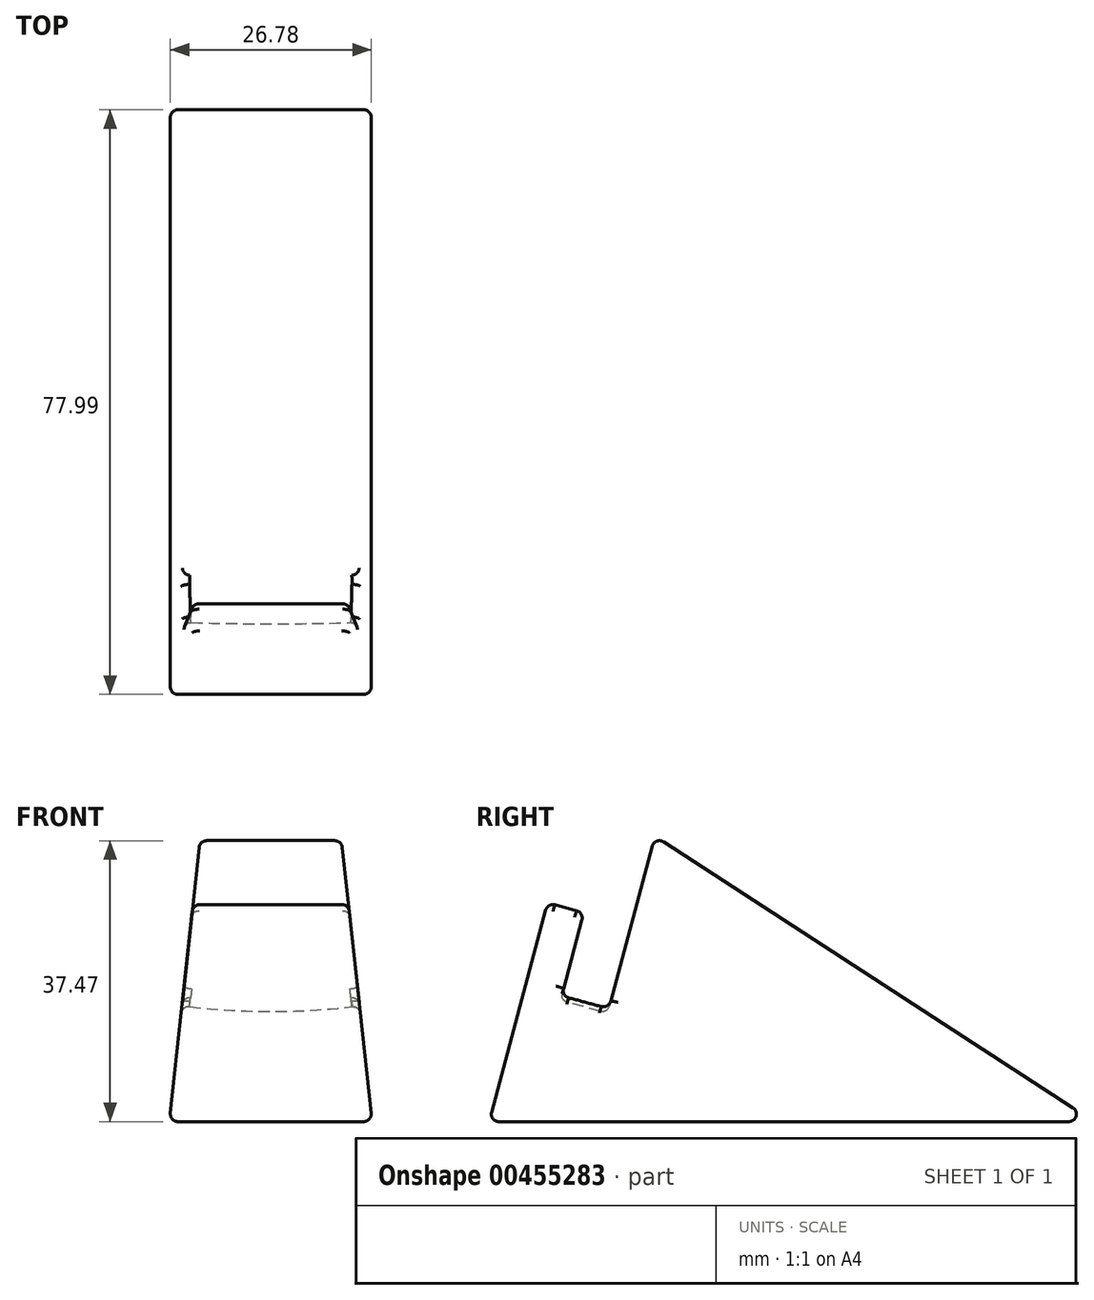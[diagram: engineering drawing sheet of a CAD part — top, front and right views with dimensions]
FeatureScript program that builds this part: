
annotation { "Feature Type Name" : "Feature", "Feature Type Description" : "" }
export const myFeature = defineFeature(function(context is Context, id is Id, definition is map)
    precondition{}
    {
        {
            var Q0;
            Q0=qCreatedBy(makeId("Right.planeOp"),FACE);
            var sketch = newSketch(context, id + "F0", { "sketchPlane" : qUnion([Q0])});
            skLineSegment(sketch, "E0.bottom", {"start": v(0, 0) * mm, "end": v(80.67, 0) * mm});
            skLineSegment(sketch, "E0.top", {"start": v(10.35, 38.64) * mm, "end": v(21.22, 38.64) * mm});
            skLineSegment(sketch, "E1", {"start": v(0, 0) * mm, "end": v(10.35, 38.64) * mm});
            skPoint(sketch, "E2", {"position": v(15.35, 38.64) * mm});
            skLineSegment(sketch, "E3", {"start": v(21.22, 38.64) * mm, "end": v(80.67, 0) * mm});
            skSolve(sketch);
        }
        {
            var Q0;
            Q0=makeQuery(id+"F0.imprint","IMPRINT",FACE,{"disambiguationData":[TD([[makeQuery(id+"F0.imprint","IMPRINT",EDGE,{"derivedFrom":sQuery(id+"F0.wireOp",EDGE,"E0.bottom")}),1.0]])]});
            extrude(context, id + "F1", {"entities" : qUnion([Q0]), "depth" : 27 * mm});
        }
        {
            var Q0;
            Q0=makeQuery(id+"F1.opExtrude","SWEPT_FACE",FACE,{"disambiguationData":[OSD([sQuery(id+"F0.wireOp",EDGE,"E1")])]});
            cPlane(context, id + "F2", {"entities" : qUnion([Q0]), "cplaneType" : CPlaneType.OFFSET, "offset" : 5 * mm, "oppositeDirection" : true, "width" : 150 * mm, "height" : 150 * mm});
        }
        {
            var Q0;
            Q0=qCreatedBy(id+"F2.planeOp",FACE);
            var sketch = newSketch(context, id + "F3", { "sketchPlane" : qUnion([Q0])});
            skPoint(sketch, "E4.0", {"position": v(13.5, 0) * mm});
            skLineSegment(sketch, "E5", {"start": v(13.5, 0) * mm, "end": v(13.5, 110) * mm, "construction": true});
            skCircle(sketch, "E6", {"center": v(13.5, 110) * mm, "radius": 91.94 * mm});
            skSolve(sketch);
        }
        {
            var Q0;
            Q0 = qSketchRegion(id + "F3", true);
            extrude(context, id + "F4", {"entities" : qUnion([Q0]), "operationType" : NewBodyOperationType.REMOVE, "oppositeDirection" : true, "depth" : 6.5 * mm});
        }
        {
            var Q0;
            Q0=makeQuery(id+"F1.opExtrude","CAP_FACE",FACE,{"disambiguationData":[OSD([sQuery(id+"F0.wireOp",EDGE,"E0.bottom"),sQuery(id+"F0.wireOp",EDGE,"E0.top"),sQuery(id+"F0.wireOp",EDGE,"E1"),sQuery(id+"F0.wireOp",EDGE,"E3")])],"isStart":true});
            var sketch = newSketch(context, id + "F5", { "sketchPlane" : qUnion([Q0])});
            skLineSegment(sketch, "E7", {"start": v(-12.65, 27.87) * mm, "end": v(-7.82, 29.17) * mm});
            skLineSegment(sketch, "E8", {"start": v(-12.65, 27.87) * mm, "end": v(-18.68, 34.78) * mm});
            skLineSegment(sketch, "E9", {"start": v(-18.68, 34.78) * mm, "end": v(-16.11, 47.32) * mm});
            skLineSegment(sketch, "E10", {"start": v(-16.11, 47.32) * mm, "end": v(-7.28, 43.61) * mm});
            skLineSegment(sketch, "E11", {"start": v(-7.28, 43.61) * mm, "end": v(-5.57, 30.5) * mm});
            skLineSegment(sketch, "E12", {"start": v(-5.57, 30.5) * mm, "end": v(-7.82, 29.17) * mm});
            skSolve(sketch);
        }
        {
            var Q0;
            {var subQ4=sQuery(id+"F5.wireOp",EDGE,"E8");Q0=makeQuery(id+"F5.imprint","IMPRINT",FACE,{"disambiguationData":[TD([[makeQuery(id+"F5.imprint","IMPRINT",EDGE,{"derivedFrom":subQ4}),-1.0]])]});}
            var Q1;
            {var subQ0=sQuery(id+"F5.wireOp",EDGE,"E7");Q1=makeQuery(id+"F5.imprint","IMPRINT",FACE,{"disambiguationData":[TD([[makeQuery(id+"F5.imprint","IMPRINT",EDGE,{"derivedFrom":subQ0}),1.0]])]});}
            extrude(context, id + "F6", {"entities" : qUnion([Q0, Q1]), "operationType" : NewBodyOperationType.REMOVE, "oppositeDirection" : true, "depth" : 43.7 * mm});
        }
        {
            var Q0;
            Q0=qCreatedBy(makeId("Front.planeOp"),FACE);
            var sketch = newSketch(context, id + "F7", { "sketchPlane" : qUnion([Q0])});
            skLineSegment(sketch, "E13", {"start": v(0, 0) * mm, "end": v(5.54, 51.24) * mm});
            skPoint(sketch, "E14.0", {"position": v(13.5, 38.06) * mm});
            skLineSegment(sketch, "E15", {"start": v(13.5, 38.06) * mm, "end": v(13.5, -10) * mm, "construction": true});
            skLineSegment(sketch, "E16.MirrorCS", {"start": v(27, 0) * mm, "end": v(21.46, 51.24) * mm});
            skLineSegment(sketch, "E17", {"start": v(5.54, 51.24) * mm, "end": v(-18.57, 42.6) * mm, "construction": true});
            skLineSegment(sketch, "E18", {"start": v(5.54, 51.24) * mm, "end": v(-20.23, 29.38) * mm});
            skLineSegment(sketch, "E19", {"start": v(-20.23, 29.38) * mm, "end": v(-22.2, -20.87) * mm});
            skLineSegment(sketch, "E20", {"start": v(-22.2, -20.87) * mm, "end": v(0, 0) * mm});
            skLineSegment(sketch, "E21", {"start": v(27, 0) * mm, "end": v(40.61, -9.3) * mm});
            skLineSegment(sketch, "E22", {"start": v(40.61, -9.3) * mm, "end": v(49.87, 59.14) * mm});
            skLineSegment(sketch, "E23", {"start": v(49.87, 59.14) * mm, "end": v(21.46, 51.24) * mm});
            skSolve(sketch);
        }
        {
            var Q0;
            Q0=makeQuery(id+"F7.imprint","IMPRINT",FACE,{"disambiguationData":[TD([[makeQuery(id+"F7.imprint","IMPRINT",EDGE,{"derivedFrom":sQuery(id+"F7.wireOp",EDGE,"E16.MirrorCS")}),-1.0]])]});
            var Q1;
            Q1=makeQuery(id+"F7.imprint","IMPRINT",FACE,{"disambiguationData":[TD([[makeQuery(id+"F7.imprint","IMPRINT",EDGE,{"derivedFrom":sQuery(id+"F7.wireOp",EDGE,"E13")}),1.0]])]});
            extrude(context, id + "F8", {"entities" : qUnion([Q0, Q1]), "operationType" : NewBodyOperationType.REMOVE, "oppositeDirection" : true, "depth" : 96 * mm});
        }
        {
            var Q0;
            Q0=makeQuery(id+"F8.boolean.opBoolean","INTERSECT",EDGE,{"derivedFrom":[makeQuery(id+"F4.boolean.opBoolean","COPY",FACE,{"derivedFrom":makeQuery(id+"F4.opExtrude","CAP_FACE",FACE,{"disambiguationData":[OSD([sQuery(id+"F3.wireOp",EDGE,"E6")])],"isStart":false})}),makeQuery(id+"F8.opExtrude","SWEPT_FACE",FACE,{"disambiguationData":[OSD([sQuery(id+"F7.wireOp",EDGE,"E13")])]})]});
            var Q1;
            Q1=makeQuery(id+"F4.boolean.opBoolean","INTERSECT",EDGE,{"derivedFrom":[makeQuery(id+"F1.opExtrude","SWEPT_FACE",FACE,{"disambiguationData":[OSD([sQuery(id+"F0.wireOp",EDGE,"E3")])]}),makeQuery(id+"F4.opExtrude","CAP_FACE",FACE,{"disambiguationData":[OSD([sQuery(id+"F3.wireOp",EDGE,"E6")])],"isStart":false})]});
            var Q2;
            Q2=makeQuery(id+"F1.opExtrude","SWEPT_FACE",FACE,{"disambiguationData":[OSD([sQuery(id+"F0.wireOp",EDGE,"E3")])]});
            var Q3;
            Q3=makeQuery(id+"F4.boolean.opBoolean","COPY",FACE,{"derivedFrom":makeQuery(id+"F4.opExtrude","CAP_FACE",FACE,{"disambiguationData":[OSD([sQuery(id+"F3.wireOp",EDGE,"E6")])],"isStart":false})});
            var Q4;
            Q4=makeQuery(id+"F8.boolean.opBoolean","INTERSECT",EDGE,{"derivedFrom":[makeQuery(id+"F4.boolean.opBoolean","COPY",FACE,{"derivedFrom":makeQuery(id+"F4.opExtrude","CAP_FACE",FACE,{"disambiguationData":[OSD([sQuery(id+"F3.wireOp",EDGE,"E6")])],"isStart":true})}),makeQuery(id+"F8.opExtrude","SWEPT_FACE",FACE,{"disambiguationData":[OSD([sQuery(id+"F7.wireOp",EDGE,"E16.MirrorCS")])]})]});
            var Q5;
            Q5=makeQuery(id+"F8.boolean.opBoolean","INTERSECT",EDGE,{"derivedFrom":[makeQuery(id+"F4.boolean.opBoolean","COPY",FACE,{"derivedFrom":makeQuery(id+"F4.opExtrude","CAP_FACE",FACE,{"disambiguationData":[OSD([sQuery(id+"F3.wireOp",EDGE,"E6")])],"isStart":false})}),makeQuery(id+"F8.opExtrude","SWEPT_FACE",FACE,{"disambiguationData":[OSD([sQuery(id+"F7.wireOp",EDGE,"E16.MirrorCS")])]})]});
            var Q6;
            Q6=makeQuery(id+"F8.boolean.opBoolean","COPY",FACE,{"derivedFrom":makeQuery(id+"F8.opExtrude","SWEPT_FACE",FACE,{"disambiguationData":[OSD([sQuery(id+"F7.wireOp",EDGE,"E16.MirrorCS")])]})});
            var Q7;
            Q7=makeQuery(id+"F1.opExtrude","SWEPT_EDGE",EDGE,{"disambiguationData":[OSD([sQuery(id+"F0.wireOp",EDGE,"E0.bottom"),sQuery(id+"F0.wireOp",EDGE,"E1")])]});
            var Q8;
            Q8=makeQuery(id+"F1.opExtrude","SWEPT_FACE",FACE,{"disambiguationData":[OSD([sQuery(id+"F0.wireOp",EDGE,"E0.bottom")])]});
            var Q9;
            Q9=makeQuery(id+"F8.boolean.opBoolean","INTERSECT",EDGE,{"derivedFrom":[makeQuery(id+"F1.opExtrude","SWEPT_FACE",FACE,{"disambiguationData":[OSD([sQuery(id+"F0.wireOp",EDGE,"E1")])]}),makeQuery(id+"F8.opExtrude","SWEPT_FACE",FACE,{"disambiguationData":[OSD([sQuery(id+"F7.wireOp",EDGE,"E16.MirrorCS")])]})]});
            var Q10;
            Q10=makeQuery(id+"F1.opExtrude","SWEPT_FACE",FACE,{"disambiguationData":[OSD([sQuery(id+"F0.wireOp",EDGE,"E1")])]});
            var Q11;
            Q11=makeQuery(id+"F8.boolean.opBoolean","INTERSECT",EDGE,{"derivedFrom":[makeQuery(id+"F1.opExtrude","SWEPT_FACE",FACE,{"disambiguationData":[OSD([sQuery(id+"F0.wireOp",EDGE,"E1")])]}),makeQuery(id+"F8.opExtrude","SWEPT_FACE",FACE,{"disambiguationData":[OSD([sQuery(id+"F7.wireOp",EDGE,"E13")])]})]});
            var Q12;
            Q12=makeQuery(id+"F4.boolean.opBoolean","COPY",EDGE,{"derivedFrom":makeQuery(id+"F4.opExtrude","CAP_EDGE",EDGE,{"disambiguationData":[OSD([sQuery(id+"F3.wireOp",EDGE,"E6")])],"isStart":false})});
            var Q13;
            Q13=makeQuery(id+"F8.boolean.opBoolean","INTERSECT",EDGE,{"derivedFrom":[makeQuery(id+"F1.opExtrude","SWEPT_FACE",FACE,{"disambiguationData":[OSD([sQuery(id+"F0.wireOp",EDGE,"E3")])]}),makeQuery(id+"F8.opExtrude","SWEPT_FACE",FACE,{"disambiguationData":[OSD([sQuery(id+"F7.wireOp",EDGE,"E13")])]})]});
            var Q14;
            Q14=makeQuery(id+"F4.boolean.opBoolean","COPY",FACE,{"derivedFrom":makeQuery(id+"F4.opExtrude","SWEPT_FACE",FACE,{"disambiguationData":[OSD([sQuery(id+"F3.wireOp",EDGE,"E6")])]})});
            var Q15;
            Q15=makeQuery(id+"F8.boolean.opBoolean","INTERSECT",EDGE,{"derivedFrom":[makeQuery(id+"F4.boolean.opBoolean","COPY",FACE,{"derivedFrom":makeQuery(id+"F4.opExtrude","SWEPT_FACE",FACE,{"disambiguationData":[OSD([sQuery(id+"F3.wireOp",EDGE,"E6")])]})}),makeQuery(id+"F8.opExtrude","SWEPT_FACE",FACE,{"disambiguationData":[OSD([sQuery(id+"F7.wireOp",EDGE,"E16.MirrorCS")])]})]});
            var Q16;
            Q16=makeQuery(id+"F8.boolean.opBoolean","INTERSECT",EDGE,{"derivedFrom":[makeQuery(id+"F1.opExtrude","SWEPT_FACE",FACE,{"disambiguationData":[OSD([sQuery(id+"F0.wireOp",EDGE,"E3")])]}),makeQuery(id+"F8.opExtrude","SWEPT_FACE",FACE,{"disambiguationData":[OSD([sQuery(id+"F7.wireOp",EDGE,"E16.MirrorCS")])]})]});
            var Q17;
            Q17=makeQuery(id+"F6.boolean.opBoolean","COPY",FACE,{"derivedFrom":makeQuery(id+"F6.opExtrude","SWEPT_FACE",FACE,{"disambiguationData":[OSD([sQuery(id+"F5.wireOp",EDGE,"E7")])]})});
            var Q18;
            Q18=makeQuery(id+"F6.boolean.opBoolean","COPY",EDGE,{"derivedFrom":makeQuery(id+"F6.opExtrude","SWEPT_EDGE",EDGE,{"disambiguationData":[OSD([sQuery(id+"F0.wireOp",EDGE,"E0.bottom"),sQuery(id+"F0.wireOp",EDGE,"E0.top"),sQuery(id+"F0.wireOp",EDGE,"E1"),sQuery(id+"F0.wireOp",EDGE,"E3"),sQuery(id+"F3.wireOp",EDGE,"E6"),sQuery(id+"F5.wireOp",EDGE,"E7"),sQuery(id+"F5.wireOp",EDGE,"E8")])]})});
            var Q19;
            Q19=makeQuery(id+"F8.boolean.opBoolean","COPY",FACE,{"derivedFrom":makeQuery(id+"F8.opExtrude","SWEPT_FACE",FACE,{"disambiguationData":[OSD([sQuery(id+"F7.wireOp",EDGE,"E13")])]})});
            var Q20;
            Q20=makeQuery(id+"F1.opExtrude","SWEPT_EDGE",EDGE,{"disambiguationData":[OSD([sQuery(id+"F0.wireOp",EDGE,"E0.bottom"),sQuery(id+"F0.wireOp",EDGE,"E3")])]});
            var Q21;
            Q21=makeQuery(id+"F8.boolean.opBoolean","MERGE",EDGE,{"derivedFrom":[makeQuery(id+"F1.opExtrude","CAP_EDGE",EDGE,{"disambiguationData":[OSD([sQuery(id+"F0.wireOp",EDGE,"E0.bottom")])],"isStart":false}),makeQuery(id+"F8.opExtrude","SWEPT_EDGE",EDGE,{"disambiguationData":[OSD([sQuery(id+"F7.wireOp",EDGE,"E16.MirrorCS"),sQuery(id+"F7.wireOp",EDGE,"E21")])]})]});
            var Q22;
            Q22=makeQuery(id+"F8.boolean.opBoolean","MERGE",EDGE,{"derivedFrom":[makeQuery(id+"F1.opExtrude","CAP_EDGE",EDGE,{"disambiguationData":[OSD([sQuery(id+"F0.wireOp",EDGE,"E0.bottom")])],"isStart":true}),makeQuery(id+"F8.opExtrude","SWEPT_EDGE",EDGE,{"disambiguationData":[OSD([sQuery(id+"F7.wireOp",EDGE,"E13"),sQuery(id+"F7.wireOp",EDGE,"E20")])]})]});
            var Q23;
            Q23=makeQuery(id+"F6.boolean.opBoolean","COPY",EDGE,{"derivedFrom":makeQuery(id+"F6.opExtrude","SWEPT_EDGE",EDGE,{"disambiguationData":[OSD([sQuery(id+"F0.wireOp",EDGE,"E1"),sQuery(id+"F5.wireOp",EDGE,"E7"),sQuery(id+"F5.wireOp",EDGE,"E12")])]})});
            var Q24;
            Q24=makeQuery(id+"F4.boolean.opBoolean","COPY",FACE,{"derivedFrom":makeQuery(id+"F4.opExtrude","CAP_FACE",FACE,{"disambiguationData":[OSD([sQuery(id+"F3.wireOp",EDGE,"E6")])],"isStart":true})});
            var Q25;
            Q25=makeQuery(id+"F4.boolean.opBoolean","COPY",EDGE,{"derivedFrom":makeQuery(id+"F4.opExtrude","CAP_EDGE",EDGE,{"disambiguationData":[OSD([sQuery(id+"F3.wireOp",EDGE,"E6")])],"isStart":true})});
            var Q26;
            Q26=makeQuery(id+"F8.boolean.opBoolean","INTERSECT",EDGE,{"derivedFrom":[makeQuery(id+"F4.boolean.opBoolean","COPY",FACE,{"derivedFrom":makeQuery(id+"F4.opExtrude","CAP_FACE",FACE,{"disambiguationData":[OSD([sQuery(id+"F3.wireOp",EDGE,"E6")])],"isStart":true})}),makeQuery(id+"F8.opExtrude","SWEPT_FACE",FACE,{"disambiguationData":[OSD([sQuery(id+"F7.wireOp",EDGE,"E13")])]})]});
            var Q27;
            Q27=makeQuery(id+"F8.boolean.opBoolean","INTERSECT",EDGE,{"derivedFrom":[makeQuery(id+"F6.boolean.opBoolean","COPY",FACE,{"derivedFrom":makeQuery(id+"F6.opExtrude","SWEPT_FACE",FACE,{"disambiguationData":[OSD([sQuery(id+"F5.wireOp",EDGE,"E7")])]})}),makeQuery(id+"F8.opExtrude","SWEPT_FACE",FACE,{"disambiguationData":[OSD([sQuery(id+"F7.wireOp",EDGE,"E13")])]})]});
            var Q28;
            Q28=makeQuery(id+"F8.boolean.opBoolean","INTERSECT",EDGE,{"derivedFrom":[makeQuery(id+"F4.boolean.opBoolean","COPY",FACE,{"derivedFrom":makeQuery(id+"F4.opExtrude","SWEPT_FACE",FACE,{"disambiguationData":[OSD([sQuery(id+"F3.wireOp",EDGE,"E6")])]})}),makeQuery(id+"F8.opExtrude","SWEPT_FACE",FACE,{"disambiguationData":[OSD([sQuery(id+"F7.wireOp",EDGE,"E13")])]})]});
            var Q29;
            Q29=makeQuery(id+"F8.boolean.opBoolean","INTERSECT",EDGE,{"derivedFrom":[makeQuery(id+"F6.boolean.opBoolean","COPY",FACE,{"derivedFrom":makeQuery(id+"F6.opExtrude","SWEPT_FACE",FACE,{"disambiguationData":[OSD([sQuery(id+"F5.wireOp",EDGE,"E7")])]})}),makeQuery(id+"F8.opExtrude","SWEPT_FACE",FACE,{"disambiguationData":[OSD([sQuery(id+"F7.wireOp",EDGE,"E16.MirrorCS")])]})]});
            fillet(context, id + "F9", {"entities" : qUnion([Q0, Q1, Q2, Q3, Q4, Q5, Q6, Q7, Q8, Q9, Q10, Q11, Q12, Q13, Q14, Q15, Q16, Q17, Q18, Q19, Q20, Q21, Q22, Q23, Q24, Q25, Q26, Q27, Q28, Q29]), "radius" : 1 * mm, "tangentPropagation" : true, "allowEdgeOverflow" : false});
        }
    });
